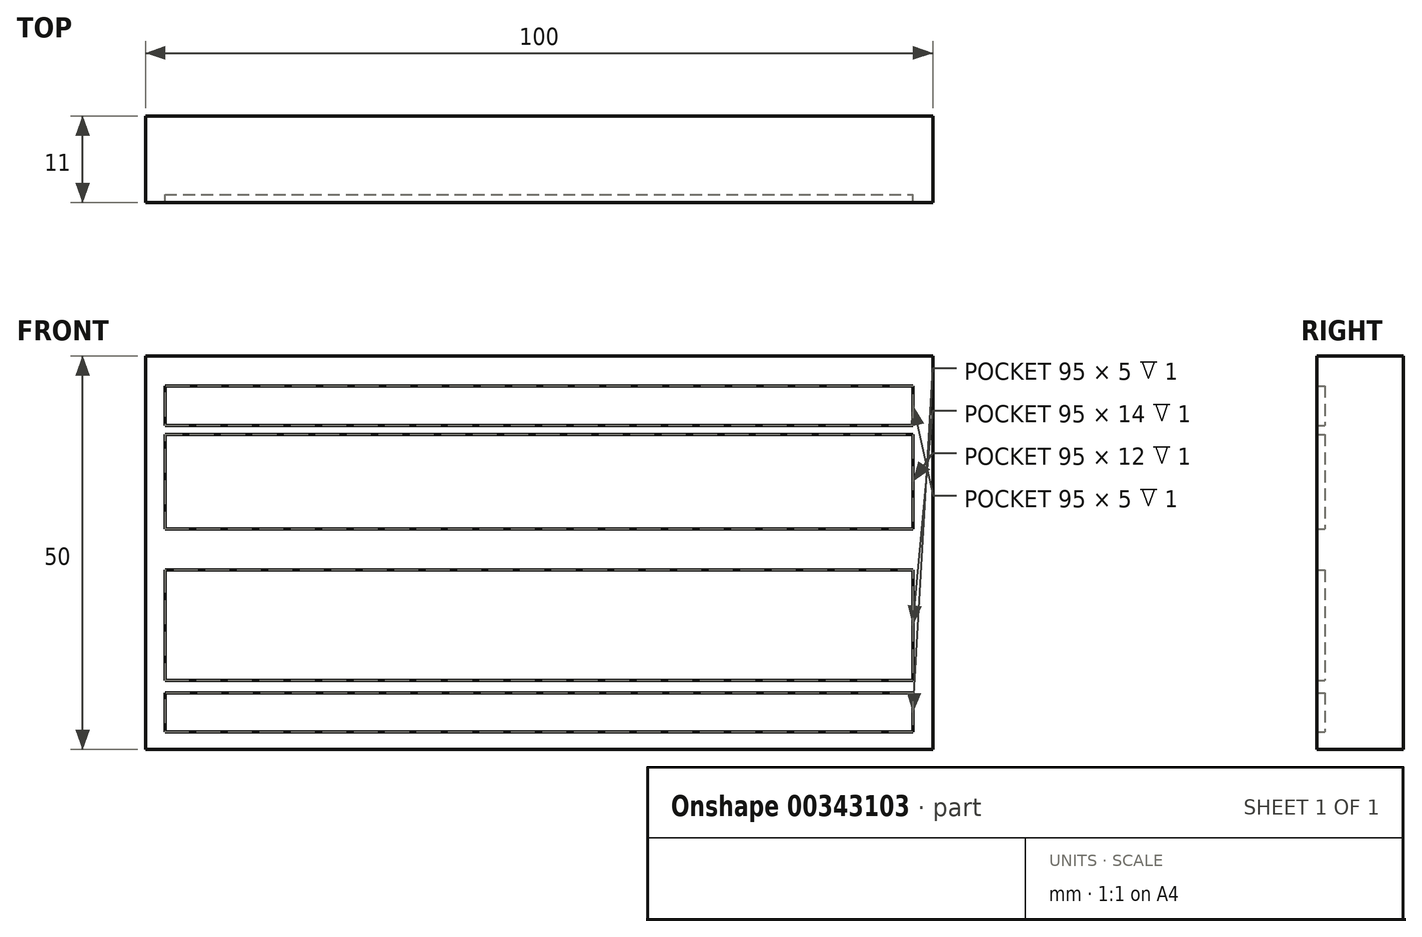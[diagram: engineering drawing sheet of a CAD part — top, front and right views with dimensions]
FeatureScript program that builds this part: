
annotation { "Feature Type Name" : "Feature", "Feature Type Description" : "" }
export const myFeature = defineFeature(function(context is Context, id is Id, definition is map)
    precondition{}
    {
        {
            var Q0;
            Q0=qCreatedBy(makeId("Front.planeOp"),FACE);
            var sketch = newSketch(context, id + "F0", { "sketchPlane" : qUnion([Q0])});
            skLineSegment(sketch, "E0.bottom", {"start": v(50, -25) * mm, "end": v(-50, -25) * mm});
            skLineSegment(sketch, "E0.top", {"start": v(50, 25) * mm, "end": v(-50, 25) * mm});
            skLineSegment(sketch, "E0.left", {"start": v(50, -25) * mm, "end": v(50, 25) * mm});
            skLineSegment(sketch, "E0.right", {"start": v(-50, -25) * mm, "end": v(-50, 25) * mm});
            skPoint(sketch, "E0.middle", {"position": v(0, 0) * mm});
            skSolve(sketch);
        }
        {
            var Q0;
            Q0 = qSketchRegion(id + "F0", true);
            extrude(context, id + "F1", {"entities" : qUnion([Q0]), "depth" : 10 * mm});
        }
        {
            var Q0;
            Q0=makeQuery(id+"F1.opExtrude","CAP_FACE",FACE,{"disambiguationData":[OSD([sQuery(id+"F0.wireOp",EDGE,"E0.bottom"),sQuery(id+"F0.wireOp",EDGE,"E0.top"),sQuery(id+"F0.wireOp",EDGE,"E0.left"),sQuery(id+"F0.wireOp",EDGE,"E0.right")])],"isStart":false});
            var sketch = newSketch(context, id + "F2", { "sketchPlane" : qUnion([Q0])});
            skLineSegment(sketch, "E1.bottom", {"start": v(-47.53, 21.2) * mm, "end": v(47.47, 21.2) * mm});
            skLineSegment(sketch, "E1.top", {"start": v(-47.53, 16.2) * mm, "end": v(47.47, 16.2) * mm});
            skLineSegment(sketch, "E1.left", {"start": v(-47.53, 21.2) * mm, "end": v(-47.53, 16.2) * mm});
            skLineSegment(sketch, "E1.right", {"start": v(47.47, 21.2) * mm, "end": v(47.47, 16.2) * mm});
            skLineSegment(sketch, "E2.bottom", {"start": v(-47.53, 15.04) * mm, "end": v(47.47, 15.04) * mm});
            skLineSegment(sketch, "E2.top", {"start": v(-47.53, 3.04) * mm, "end": v(47.47, 3.04) * mm});
            skLineSegment(sketch, "E2.left", {"start": v(-47.53, 15.04) * mm, "end": v(-47.53, 3.04) * mm});
            skLineSegment(sketch, "E2.right", {"start": v(47.47, 15.04) * mm, "end": v(47.47, 3.04) * mm});
            skLineSegment(sketch, "E3.bottom", {"start": v(-47.53, -2.2) * mm, "end": v(47.47, -2.2) * mm});
            skLineSegment(sketch, "E3.top", {"start": v(-47.53, -16.2) * mm, "end": v(47.47, -16.2) * mm});
            skLineSegment(sketch, "E3.left", {"start": v(-47.53, -2.2) * mm, "end": v(-47.53, -16.2) * mm});
            skLineSegment(sketch, "E3.right", {"start": v(47.47, -2.2) * mm, "end": v(47.47, -16.2) * mm});
            skLineSegment(sketch, "E4.bottom", {"start": v(-47.53, -17.78) * mm, "end": v(47.47, -17.78) * mm});
            skLineSegment(sketch, "E4.top", {"start": v(-47.53, -22.78) * mm, "end": v(47.47, -22.78) * mm});
            skLineSegment(sketch, "E4.left", {"start": v(-47.53, -17.78) * mm, "end": v(-47.53, -22.78) * mm});
            skLineSegment(sketch, "E4.right", {"start": v(47.47, -17.78) * mm, "end": v(47.47, -22.78) * mm});
            skSolve(sketch);
        }
        {
            var Q0;
            Q0=makeQuery(id+"F2.imprint","IMPRINT",FACE,{"disambiguationData":[TD([[makeQuery(id+"F2.imprint","IMPRINT",EDGE,{"derivedFrom":sQuery(id+"F2.wireOp",EDGE,"E1.bottom")}),1.0]])]});
            extrude(context, id + "F3", {"entities" : qUnion([Q0]), "operationType" : NewBodyOperationType.ADD, "depth" : 1 * mm});
        }
    });
